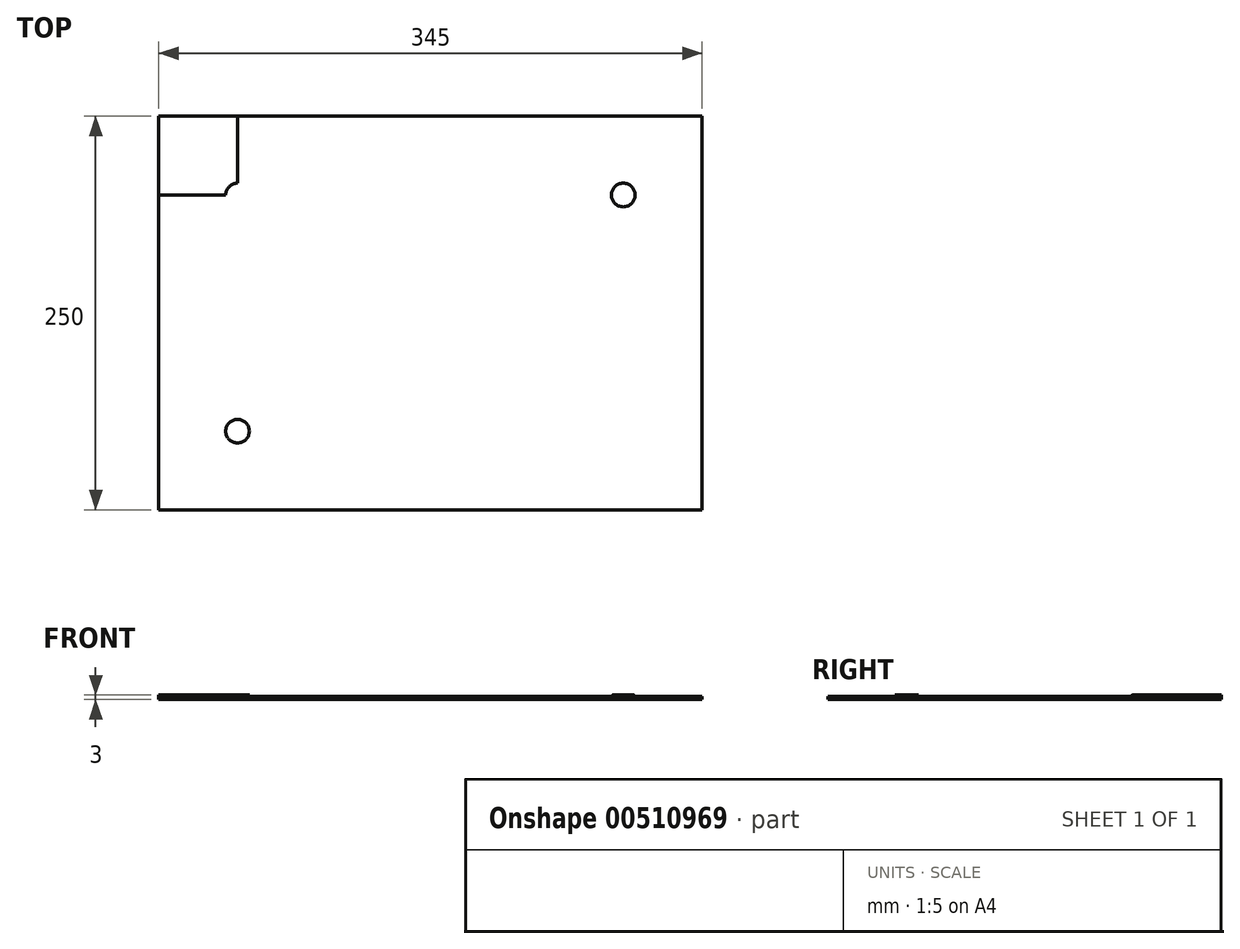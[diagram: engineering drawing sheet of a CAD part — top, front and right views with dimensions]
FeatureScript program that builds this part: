
annotation { "Feature Type Name" : "Feature", "Feature Type Description" : "" }
export const myFeature = defineFeature(function(context is Context, id is Id, definition is map)
    precondition{}
    {
        {
            var Q0;
            Q0=qCreatedBy(makeId("Top.planeOp"),FACE);
            var sketch = newSketch(context, id + "F0", { "sketchPlane" : qUnion([Q0])});
            skLineSegment(sketch, "E0.bottom", {"start": v(-172.5, -125) * mm, "end": v(172.5, -125) * mm});
            skLineSegment(sketch, "E0.top", {"start": v(-172.5, 125) * mm, "end": v(172.5, 125) * mm});
            skLineSegment(sketch, "E0.left", {"start": v(-172.5, -125) * mm, "end": v(-172.5, 125) * mm});
            skLineSegment(sketch, "E0.right", {"start": v(172.5, -125) * mm, "end": v(172.5, 125) * mm});
            skPoint(sketch, "E0.middle", {"position": v(0, 0) * mm});
            skSolve(sketch);
        }
        {
            var Q0;
            Q0=makeQuery(id+"F0.imprint","IMPRINT",FACE,{"disambiguationData":[TD([[makeQuery(id+"F0.imprint","IMPRINT",EDGE,{"derivedFrom":sQuery(id+"F0.wireOp",EDGE,"E0.bottom")}),1.0]])]});
            extrude(context, id + "F1", {"entities" : qUnion([Q0]), "depth" : 3 * mm, "offsetDistance" : 25 * mm});
        }
        {
            var Q0;
            Q0=makeQuery(id+"F1.opExtrude","CAP_FACE",FACE,{"disambiguationData":[OSD([sQuery(id+"F0.wireOp",EDGE,"E0.bottom"),sQuery(id+"F0.wireOp",EDGE,"E0.top"),sQuery(id+"F0.wireOp",EDGE,"E0.left"),sQuery(id+"F0.wireOp",EDGE,"E0.right")])],"isStart":false});
            var sketch = newSketch(context, id + "F2", { "sketchPlane" : qUnion([Q0])});
            skLineSegment(sketch, "E1.bottom", {"start": v(-172.5, 125) * mm, "end": v(-122.5, 125) * mm});
            skLineSegment(sketch, "E1.top", {"start": v(-172.5, 75) * mm, "end": v(-122.5, 75) * mm});
            skLineSegment(sketch, "E1.left", {"start": v(-172.5, 125) * mm, "end": v(-172.5, 75) * mm});
            skLineSegment(sketch, "E1.right", {"start": v(-122.5, 125) * mm, "end": v(-122.5, 75) * mm});
            skCircle(sketch, "E2", {"center": v(-122.5, 75) * mm, "radius": 7.5 * mm});
            skCircle(sketch, "E3.MirrorC", {"center": v(122.5, 75) * mm, "radius": 7.5 * mm});
            skCircle(sketch, "E4.MirrorC", {"center": v(-122.5, -75) * mm, "radius": 7.5 * mm});
            skCircle(sketch, "E5.MirrorC", {"center": v(122.5, -75) * mm, "radius": 7.5 * mm});
            skSolve(sketch);
        }
        {
            var Q0;
            {var subQ0=sQuery(id+"F2.wireOp",EDGE,"E1.right");var subQ1=sQuery(id+"F2.wireOp",EDGE,"E1.top");var subQ2=makeQuery(id+"F2.imprint","INTERSECT",VERTEX,{"derivedFrom":[subQ1,subQ0]});Q0=makeQuery(id+"F2.imprint","IMPRINT",FACE,{"disambiguationData":[TD([[makeQuery(id+"F2.imprint","IMPRINT",EDGE,{"disambiguationData":[TD([[subQ2,1.0]])],"derivedFrom":subQ1}),1.0]])]});}
            var Q1;
            {var subQ0=sQuery(id+"F2.wireOp",EDGE,"E1.right");var subQ1=sQuery(id+"F2.wireOp",EDGE,"E1.top");var subQ2=makeQuery(id+"F2.imprint","INTERSECT",VERTEX,{"derivedFrom":[subQ1,subQ0]});Q1=makeQuery(id+"F2.imprint","IMPRINT",FACE,{"disambiguationData":[TD([[makeQuery(id+"F2.imprint","IMPRINT",EDGE,{"disambiguationData":[TD([[subQ2,1.0]])],"derivedFrom":subQ1}),-1.0]])]});}
            var Q2;
            Q2=makeQuery(id+"F2.imprint","IMPRINT",FACE,{"disambiguationData":[TD([[makeQuery(id+"F2.imprint","IMPRINT",EDGE,{"derivedFrom":sQuery(id+"F2.wireOp",EDGE,"E3.MirrorC")}),-1.0]])]});
            var Q3;
            Q3=makeQuery(id+"F2.imprint","IMPRINT",FACE,{"disambiguationData":[TD([[makeQuery(id+"F2.imprint","IMPRINT",EDGE,{"derivedFrom":sQuery(id+"F2.wireOp",EDGE,"E5.MirrorC")}),1.0]])]});
            var Q4;
            Q4=makeQuery(id+"F2.imprint","IMPRINT",FACE,{"disambiguationData":[TD([[makeQuery(id+"F2.imprint","IMPRINT",EDGE,{"derivedFrom":sQuery(id+"F2.wireOp",EDGE,"E4.MirrorC")}),-1.0]])]});
            extrude(context, id + "F3", {"entities" : qUnion([Q0, Q1, Q2, Q3, Q4]), "operationType" : NewBodyOperationType.REMOVE, "oppositeDirection" : true, "depth" : 1 * mm, "offsetDistance" : 25 * mm});
        }
        {
            var Q0;
            Q0=makeQuery(id+"F3.boolean.opBoolean","COPY",EDGE,{"derivedFrom":makeQuery(id+"F3.opExtrude","CAP_EDGE",EDGE,{"disambiguationData":[OSD([sQuery(id+"F2.wireOp",EDGE,"E2")])],"isStart":true})});
            var Q1;
            Q1=makeQuery(id+"F3.boolean.opBoolean","COPY",EDGE,{"derivedFrom":makeQuery(id+"F3.opExtrude","CAP_EDGE",EDGE,{"disambiguationData":[OSD([sQuery(id+"F2.wireOp",EDGE,"E4.MirrorC")])],"isStart":true})});
            var Q2;
            Q2=makeQuery(id+"F3.boolean.opBoolean","COPY",EDGE,{"derivedFrom":makeQuery(id+"F3.opExtrude","CAP_EDGE",EDGE,{"disambiguationData":[OSD([sQuery(id+"F2.wireOp",EDGE,"E5.MirrorC")])],"isStart":true})});
            var Q3;
            Q3=makeQuery(id+"F3.boolean.opBoolean","COPY",EDGE,{"derivedFrom":makeQuery(id+"F3.opExtrude","CAP_EDGE",EDGE,{"disambiguationData":[OSD([sQuery(id+"F2.wireOp",EDGE,"E3.MirrorC")])],"isStart":true})});
            fillet(context, id + "F4", {"entities" : qUnion([Q0, Q1, Q2, Q3]), "radius" : 1.5 * mm, "tangentPropagation" : true, "allowEdgeOverflow" : false});
        }
    });
